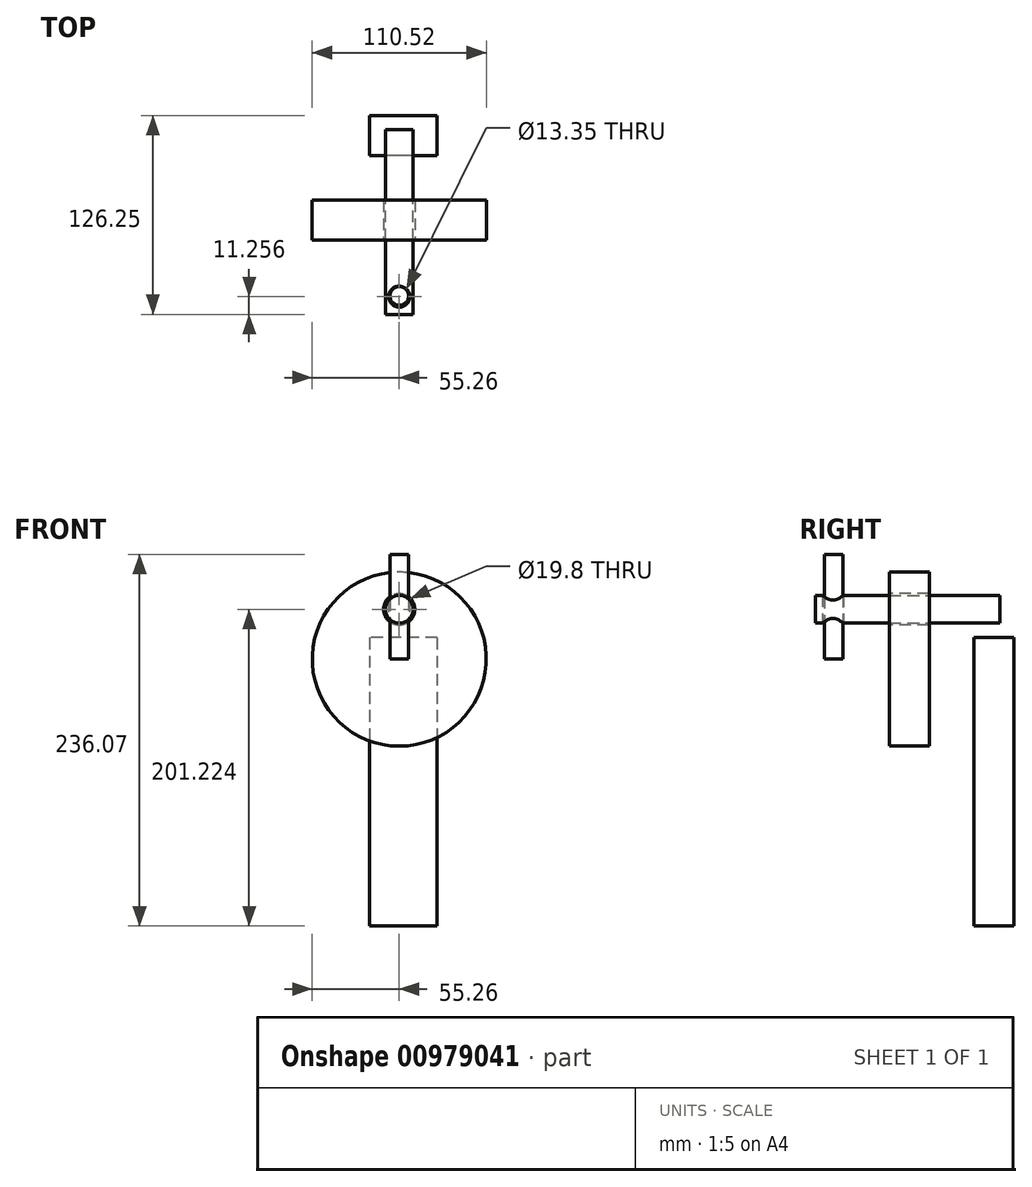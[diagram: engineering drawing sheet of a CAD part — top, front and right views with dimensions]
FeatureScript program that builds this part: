
annotation { "Feature Type Name" : "Feature", "Feature Type Description" : "" }
export const myFeature = defineFeature(function(context is Context, id is Id, definition is map)
    precondition{}
    {
        {
            var Q0;
            Q0=qCreatedBy(makeId("Front.planeOp"),FACE);
            var sketch = newSketch(context, id + "F0", { "sketchPlane" : qUnion([Q0])});
            skCircle(sketch, "E0", {"center": v(0, 0) * mm, "radius": 55.26 * mm});
            skSolve(sketch);
        }
        {
            var Q0;
            Q0=makeQuery(id+"F0.imprint","IMPRINT",FACE,{"disambiguationData":[TD([[makeQuery(id+"F0.imprint","IMPRINT",EDGE,{"derivedFrom":sQuery(id+"F0.wireOp",EDGE,"E0")}),1.0]])]});
            extrude(context, id + "F1", {"entities" : qUnion([Q0]), "depth" : 25.4 * mm, "offsetDistance" : 25.4 * mm});
        }
        {
            var Q0;
            Q0=makeQuery(id+"F1.opExtrude","CAP_FACE",FACE,{"disambiguationData":[OSD([sQuery(id+"F0.wireOp",EDGE,"E0")])],"isStart":false});
            var sketch = newSketch(context, id + "F2", { "sketchPlane" : qUnion([Q0])});
            skLineSegment(sketch, "E1", {"start": v(0, 0) * mm, "end": v(0, 160.85) * mm, "construction": true});
            skLineSegment(sketch, "E2", {"start": v(0, 0) * mm, "end": v(0, -86.97) * mm, "construction": true});
            skCircle(sketch, "E3", {"center": v(0, 31.67) * mm, "radius": 9.9 * mm});
            skSolve(sketch);
        }
        {
            var Q0;
            Q0=makeQuery(id+"F2.imprint","IMPRINT",FACE,{"disambiguationData":[TD([[makeQuery(id+"F2.imprint","IMPRINT",EDGE,{"derivedFrom":sQuery(id+"F2.wireOp",EDGE,"E3")}),1.0]])]});
            extrude(context, id + "F3", {"entities" : qUnion([Q0]), "operationType" : NewBodyOperationType.REMOVE, "oppositeDirection" : true, "depth" : 116.45 * mm, "offsetDistance" : 25.4 * mm});
        }
        {
            var Q0;
            Q0=makeQuery(id+"F1.opExtrude","CAP_FACE",FACE,{"disambiguationData":[OSD([sQuery(id+"F0.wireOp",EDGE,"E0")])],"isStart":false});
            var sketch = newSketch(context, id + "F4", { "sketchPlane" : qUnion([Q0])});
            skCircle(sketch, "E4", {"center": v(0, 31.67) * mm, "radius": 8.81 * mm});
            skSolve(sketch);
        }
        {
            var Q0;
            Q0=makeQuery(id+"F4.imprint","IMPRINT",FACE,{"disambiguationData":[TD([[makeQuery(id+"F4.imprint","IMPRINT",EDGE,{"derivedFrom":sQuery(id+"F4.wireOp",EDGE,"E4")}),1.0]])]});
            extrude(context, id + "F5", {"entities" : qUnion([Q0]), "depth" : 47.03 * mm, "offsetDistance" : 25.4 * mm});
        }
        {
            var Q0;
            Q0=makeQuery(id+"F5.opExtrude","CAP_FACE",FACE,{"disambiguationData":[OSD([sQuery(id+"F4.wireOp",EDGE,"E4")])],"isStart":true});
            extrude(context, id + "F6", {"entities" : qUnion([Q0]), "operationType" : NewBodyOperationType.ADD, "depth" : 70.3 * mm, "offsetDistance" : 25.4 * mm});
        }
        {
            var Q0;
            Q0=qCreatedBy(makeId("Top.planeOp"),FACE);
            var sketch = newSketch(context, id + "F7", { "sketchPlane" : qUnion([Q0])});
            skLineSegment(sketch, "E5", {"start": v(0, 53.82) * mm, "end": v(0, -100.71) * mm, "construction": true});
            skSolve(sketch);
        }
        {
            var Q0;
            Q0=qCreatedBy(makeId("Top.planeOp"),FACE);
            var sketch = newSketch(context, id + "F8", { "sketchPlane" : qUnion([Q0])});
            skCircle(sketch, "E6", {"center": v(0, -61.17) * mm, "radius": 6.68 * mm});
            skSolve(sketch);
        }
        {
            var Q0;
            Q0=makeQuery(id+"F8.imprint","IMPRINT",FACE,{"disambiguationData":[TD([[makeQuery(id+"F8.imprint","IMPRINT",EDGE,{"derivedFrom":sQuery(id+"F8.wireOp",EDGE,"E6")}),1.0]])]});
            extrude(context, id + "F9", {"entities" : qUnion([Q0]), "operationType" : NewBodyOperationType.REMOVE, "depth" : 74.2 * mm, "offsetDistance" : 25.4 * mm});
        }
        {
            var Q0;
            Q0=qCreatedBy(makeId("Top.planeOp"),FACE);
            var sketch = newSketch(context, id + "F10", { "sketchPlane" : qUnion([Q0])});
            skCircle(sketch, "E7", {"center": v(0, -60.74) * mm, "radius": 5.93 * mm});
            skSolve(sketch);
        }
        {
            var Q0;
            Q0=makeQuery(id+"F10.imprint","IMPRINT",FACE,{"disambiguationData":[TD([[makeQuery(id+"F10.imprint","IMPRINT",EDGE,{"derivedFrom":sQuery(id+"F10.wireOp",EDGE,"E7")}),1.0]])]});
            extrude(context, id + "F11", {"entities" : qUnion([Q0]), "depth" : 66.52 * mm, "offsetDistance" : 25.4 * mm});
        }
        {
            var Q0;
            Q0=qCreatedBy(makeId("Front.planeOp"),FACE);
            var Q1;
            Q1=sQuery(id+"F7.wireOp",VERTEX,"E5.start");
            cPlane(context, id + "F12", {"entities" : qUnion([Q0, Q1]), "cplaneType" : CPlaneType.PLANE_POINT, "offset" : 25.4 * mm, "width" : 152.4 * mm, "height" : 152.4 * mm});
        }
        {
            var Q0;
            Q0=qCreatedBy(id+"F12.planeOp",FACE);
            var sketch = newSketch(context, id + "F13", { "sketchPlane" : qUnion([Q0])});
            skLineSegment(sketch, "E8.bottom", {"start": v(24.1, 13.64) * mm, "end": v(-18.88, 13.64) * mm});
            skLineSegment(sketch, "E8.top", {"start": v(24.1, -169.55) * mm, "end": v(-18.88, -169.55) * mm});
            skLineSegment(sketch, "E8.left", {"start": v(24.1, 13.64) * mm, "end": v(24.1, -169.55) * mm});
            skLineSegment(sketch, "E8.right", {"start": v(-18.88, 13.64) * mm, "end": v(-18.88, -169.55) * mm});
            skSolve(sketch);
        }
        {
            var Q0;
            Q0=makeQuery(id+"F13.imprint","IMPRINT",FACE,{"disambiguationData":[TD([[makeQuery(id+"F13.imprint","IMPRINT",EDGE,{"derivedFrom":sQuery(id+"F13.wireOp",EDGE,"E8.bottom")}),1.0]])]});
            extrude(context, id + "F14", {"entities" : qUnion([Q0]), "depth" : 25.4 * mm, "offsetDistance" : 25.4 * mm});
        }
    });
